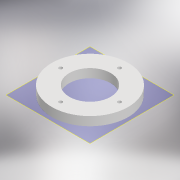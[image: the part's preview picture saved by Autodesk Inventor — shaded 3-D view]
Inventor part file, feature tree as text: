
AUTODESK INVENTOR PART (.ipt)
format: ipt  version: 2021 (Build 250183000, 183)  size: 133,632 bytes
history: native  units: mm
features: extrude x3, sketch x3, mirror x1, plane x1
ambient origin geometry x8: Origin, YZ Plane, XZ Plane, XY Plane, X Axis, Y Axis, Z Axis, Center Point
bodies: Solid1 (feature_tree)
feature tree (8):
  extrude  "Extrusion1"  Depth=87.0mm
  extrude  "Extrusion2"  Depth=10.0mm
  mirror  "Mirror1"
  extrude  "Extrusion3"  Depth=10.0mm
  plane  "Work Plane1"
  sketch  "Sketch1"  dims[d0=47.0mm d1=87.0mm]
  sketch  "Sketch2"  dims[d2=10.0mm d3=0.0mm d4=4.0mm]
  sketch  "Sketch3"  dims[d5=10.0mm d6=0.0mm d7=4.0mm d8=4.0mm d9=10.0mm d10=0.0mm d11=0.0mm]
